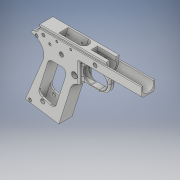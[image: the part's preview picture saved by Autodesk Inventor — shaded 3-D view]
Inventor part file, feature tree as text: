
AUTODESK INVENTOR PART (.ipt)
format: ipt  version: 2018.3 (Build 223284000, 284)  size: 622,592 bytes
history: native  units: in
note: dims shown in document units (in); Inventor stores cm internally (conversion verified against a paired STEP export)
features: extrude x9, sketch x8, plane x4, fillet x2, chamfer x1
ambient origin geometry x8: Origin, YZ Plane, XZ Plane, XY Plane, X Axis, Y Axis, Z Axis, Center Point
bodies: Solid1 (feature_tree)
feature tree (24):
  sketch  "Sketch1"  dims[d0=0.03in d1=0.849in]
  extrude  "Extrusion1"  Depth=0.849in
  chamfer  "Chamfer1"  Distance=3.03in
  plane  "Work Plane1"
  sketch  "Sketch2"  dims[d2=0.424in]
  extrude  "Extrusion2"  Depth=0.484in
  sketch  "Sketch3"  dims[d3=2.66in]
  plane  "Work Plane2"
  extrude  "Extrusion3"  Depth=0.484in
  extrude  "Extrusion4"  Depth=0.484in
  fillet  "Fillet1"  Radius=0.5in
  fillet  "Fillet2"  Radius=0.5in
  plane  "Work Plane3"
  extrude  "Extrusion5"  Depth=0.484in
  extrude  "Extrusion6"  Depth=0.484in
  plane  "Work Plane4"
  extrude  "Extrusion7"  Depth=0.484in
  sketch  "Sketch9"  dims[d9=0.1202in]
  extrude  "Extrusion8"  Depth=0.484in
  extrude  "Extrusion9"  Depth=0.484in
  sketch  "Sketch4"  dims[d4=0.59in]
  sketch  "Sketch6"  dims[d6=0.44in]
  sketch  "Sketch8"  dims[d7=0.924in]
  sketch  "Sketch12"  dims[d10=1.28in d11=3.03in d12=2.88in d13=0.5in d14=0.5in d15=0.5in d16=0.5in d17=1.031in d18=0.26in d19=0.0577in d20=0.795in d21=0.138in d22=0.21in d23=22.5deg d24=0.924in d26=0.56in d27=0.75in d28=1.229in d29=0.016in d30=0.1567in d31=0.905in d32=0.345in d33=0.5944in d34=0.27in d35=0.47in d36=0.565in d37=0.29in d39=0.45in d40=0.32in d41=3.745in d42=0.157in d43=0.201in d44=0.2179in d45=3.018in d46=3.309in d47=3.595in d48=0.313in d49=1.095in d50=1.193in d51=0.2179in d52=1.937in d53=0.431in d54=0.0988in d55=0.0988in d56=0.8016in d57=1.402in d58=0.076in d59=0.0625in d60=2.328in d61=0.307in d62=0.1575in d63=2.973in d64=0.1558in d65=3.368in d66=0.21in d67=0.11in d68=2.602in d69=0.252in d70=0.762in d71=0.0in d72=0.015in d73=0.125in d74=0.0016in d75=0.0in d76=0.751in d77=0.1in d78=0.314in d79=0.314in d80=0.119in d81=0.449in d82=0.45in d83=0.089in d84=0.762in d85=0.0in d86=0.82in d87=0.658in d97=0.658in d98=0.631in d99=3.0in d100=0.0in d101=0.089in d102=1.0in d103=0.1835in d104=0.1835in d105=3.5745in d106=0.0in d107=0.1in d109=0.02in d110=0.08in d113=0.551in d114=1.106in d115=1.0in d116=0.0in d117=1.0in d118=0.431in d119=0.0in d120=0.0in d121=0.089in d122=0.449in d123=0.365in d124=1.0in d125=0.0in d127=0.25in d128=0.0in d132=2.526in d133=0.484in d134=0.215in d135=6.75in d136=0.0in]
